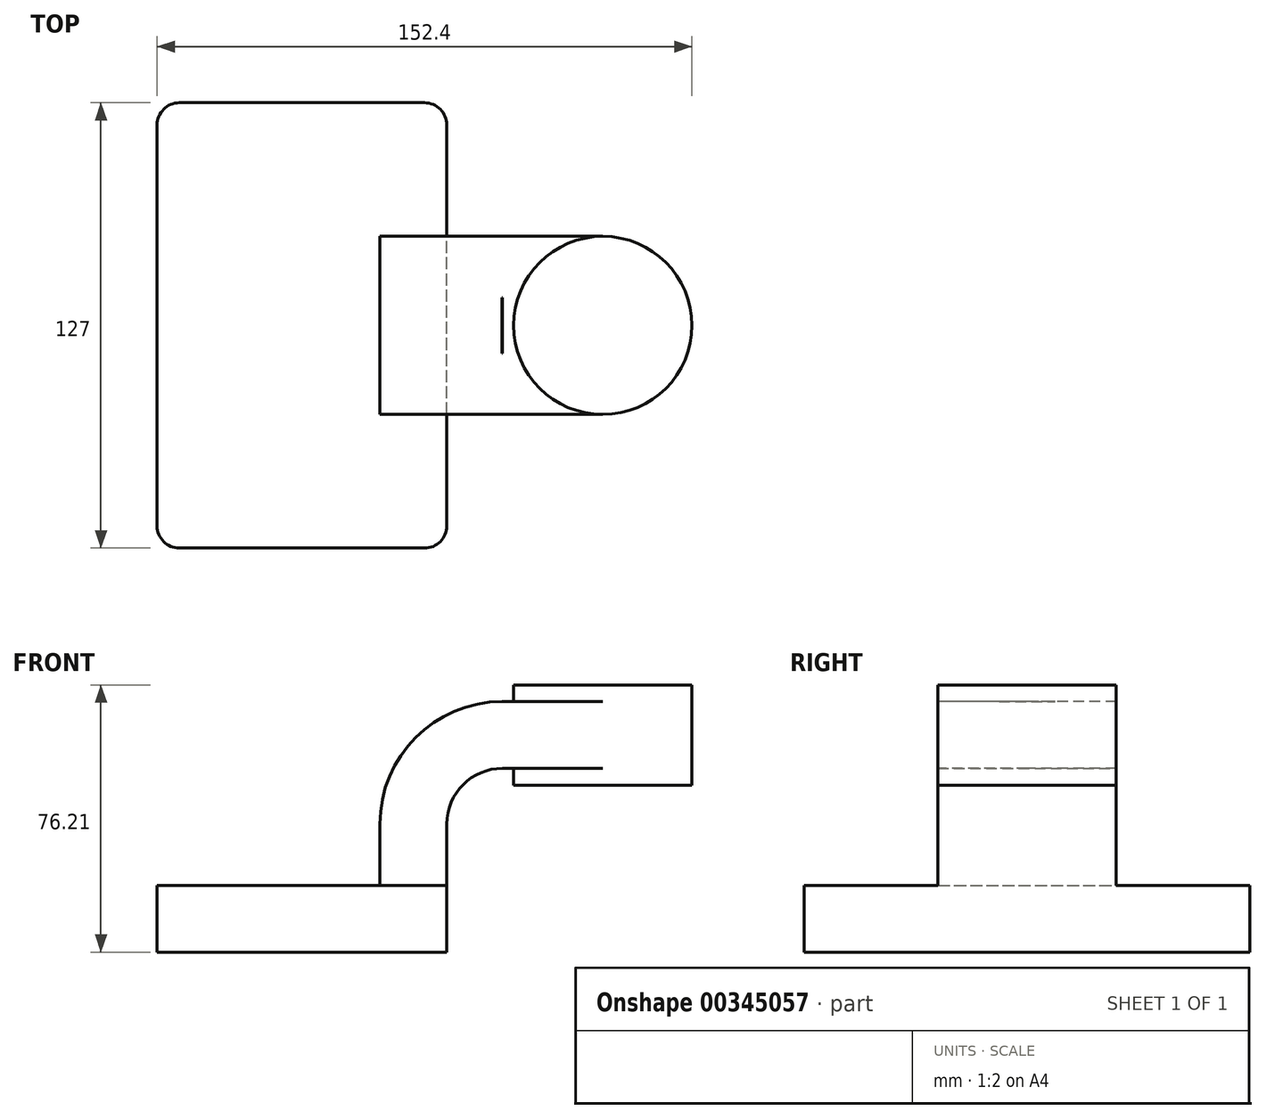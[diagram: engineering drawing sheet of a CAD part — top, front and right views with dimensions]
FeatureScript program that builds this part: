
annotation { "Feature Type Name" : "Feature", "Feature Type Description" : "" }
export const myFeature = defineFeature(function(context is Context, id is Id, definition is map)
    precondition{}
    {
        {
            var Q0;
            Q0=qCreatedBy(makeId("Front.planeOp"),FACE);
            var sketch = newSketch(context, id + "F0", { "sketchPlane" : qUnion([Q0])});
            skLineSegment(sketch, "E0.bottom", {"start": v(41.28, -9.52) * mm, "end": v(-41.28, -9.53) * mm});
            skLineSegment(sketch, "E0.top", {"start": v(41.28, 9.53) * mm, "end": v(-41.28, 9.53) * mm});
            skLineSegment(sketch, "E0.left", {"start": v(41.28, -9.52) * mm, "end": v(41.28, 9.53) * mm});
            skLineSegment(sketch, "E0.right", {"start": v(-41.28, -9.53) * mm, "end": v(-41.28, 9.53) * mm});
            skPoint(sketch, "E0.middle", {"position": v(0, 0) * mm});
            skLineSegment(sketch, "E1.bottom", {"start": v(60.32, 38.1) * mm, "end": v(111.12, 38.1) * mm});
            skLineSegment(sketch, "E1.top", {"start": v(60.32, 66.68) * mm, "end": v(111.12, 66.68) * mm});
            skLineSegment(sketch, "E1.left", {"start": v(60.32, 38.1) * mm, "end": v(60.32, 66.68) * mm});
            skLineSegment(sketch, "E1.right", {"start": v(111.12, 38.1) * mm, "end": v(111.12, 66.68) * mm});
            skPoint(sketch, "E1.middle", {"position": v(85.72, 52.39) * mm});
            skLineSegment(sketch, "E2", {"start": v(41.28, 9.53) * mm, "end": v(41.28, 27) * mm});
            skArc(sketch, "E3", {"start": v(41.27, 27) * mm, "mid": v(45.92, 38.23) * mm, "end": v(57.15, 42.88) * mm});
            skLineSegment(sketch, "E4", {"start": v(57.15, 42.88) * mm, "end": v(85.72, 42.88) * mm});
            skLineSegment(sketch, "E5.0", {"start": v(57.15, 61.93) * mm, "end": v(85.72, 61.93) * mm});
            skArc(sketch, "E5.1", {"start": v(22.23, 27) * mm, "mid": v(32.45, 51.7) * mm, "end": v(57.15, 61.93) * mm});
            skLineSegment(sketch, "E5.2", {"start": v(22.22, 9.53) * mm, "end": v(22.22, 27) * mm});
            skLineSegment(sketch, "E6", {"start": v(85.72, 42.88) * mm, "end": v(85.72, 61.93) * mm});
            skFitSpline(sketch, "E7", {"points": [v(-41.28, 9.52) * mm, v(57.15, 61.93) * mm], "startDerivative": vector(-0.5, 64.67) * mm, "endDerivative": vector(125.26, 0.2) * mm});
            skLineSegment(sketch, "E8", {"start": v(85.72, 38.1) * mm, "end": v(85.72, 66.68) * mm});
            skSolve(sketch);
        }
        {
            var Q0;
            Q0=makeQuery(id+"F0.imprint","IMPRINT",FACE,{"disambiguationData":[TD([[makeQuery(id+"F0.imprint","IMPRINT",EDGE,{"derivedFrom":sQuery(id+"F0.wireOp",EDGE,"E0.bottom")}),-1.0]])]});
            extrude(context, id + "F1", {"entities" : qUnion([Q0]), "endBound" : BoundingType.SYMMETRIC, "depth" : 127 * mm});
        }
        {
            var Q0;
            {var subQ1=sQuery(id+"F0.wireOp",EDGE,"E2");Q0=makeQuery(id+"F0.imprint","IMPRINT",FACE,{"disambiguationData":[TD([[makeQuery(id+"F0.imprint","IMPRINT",EDGE,{"derivedFrom":subQ1}),1.0]])]});}
            var Q1;
            {var subQ5=sQuery(id+"F0.wireOp",EDGE,"E6");Q1=makeQuery(id+"F0.imprint","IMPRINT",FACE,{"disambiguationData":[TD([[makeQuery(id+"F0.imprint","IMPRINT",EDGE,{"derivedFrom":subQ5}),1.0]])]});}
            extrude(context, id + "F2", {"entities" : qUnion([Q0, Q1]), "operationType" : NewBodyOperationType.ADD, "endBound" : BoundingType.SYMMETRIC, "depth" : 50.8 * mm});
        }
        {
            var Q0;
            Q0=makeQuery(id+"F0.imprint","IMPRINT",FACE,{"disambiguationData":[TD([[makeQuery(id+"F0.imprint","IMPRINT",EDGE,{"derivedFrom":sQuery(id+"F0.wireOp",EDGE,"E5.1")}),1.0]])]});
            extrude(context, id + "F3", {"entities" : qUnion([Q0]), "endBound" : BoundingType.SYMMETRIC, "depth" : 15.88 * mm});
        }
        {
            var Q0;
            {var subQ0=sQuery(id+"F0.wireOp",EDGE,"E4");var subQ1=sQuery(id+"F0.wireOp",EDGE,"E1.left");var subQ2=makeQuery(id+"F0.imprint","INTERSECT",VERTEX,{"derivedFrom":[subQ1,subQ0]});Q0=makeQuery(id+"F0.imprint","IMPRINT",FACE,{"disambiguationData":[TD([[makeQuery(id+"F0.imprint","IMPRINT",EDGE,{"disambiguationData":[TD([[subQ2,-1.0]])],"derivedFrom":subQ1}),-1.0]])]});}
            extrude(context, id + "F4", {"entities" : qUnion([Q0]), "operationType" : NewBodyOperationType.ADD, "endBound" : BoundingType.SYMMETRIC, "depth" : 50.8 * mm});
        }
        {
            var Q0;
            {var subQ4=sQuery(id+"F0.wireOp",EDGE,"E1.right");Q0=makeQuery(id+"F0.imprint","IMPRINT",FACE,{"disambiguationData":[TD([[makeQuery(id+"F0.imprint","IMPRINT",EDGE,{"derivedFrom":subQ4}),1.0]])]});}
            var Q1;
            Q1=sQuery(id+"F0.wireOp",EDGE,"E8");
            revolve(context, id + "F5", {"operationType" : NewBodyOperationType.ADD, "entities" : qUnion([Q0]), "axis" : qUnion([Q1]), "revolveType" : RevolveType.FULL});
        }
        {
            var Q0;
            Q0=makeQuery(id+"F1.opExtrude","CAP_EDGE",EDGE,{"disambiguationData":[OSD([sQuery(id+"F0.wireOp",EDGE,"E0.right")])],"isStart":false});
            var Q1;
            Q1=makeQuery(id+"F1.opExtrude","CAP_EDGE",EDGE,{"disambiguationData":[OSD([sQuery(id+"F0.wireOp",EDGE,"E0.left")])],"isStart":false});
            var Q2;
            Q2=makeQuery(id+"F1.opExtrude","CAP_EDGE",EDGE,{"disambiguationData":[OSD([sQuery(id+"F0.wireOp",EDGE,"E0.left")])],"isStart":true});
            var Q3;
            Q3=makeQuery(id+"F1.opExtrude","CAP_EDGE",EDGE,{"disambiguationData":[OSD([sQuery(id+"F0.wireOp",EDGE,"E0.right")])],"isStart":true});
            fillet(context, id + "F6", {"entities" : qUnion([Q0, Q1, Q2, Q3]), "radius" : 6.35 * mm, "tangentPropagation" : true, "allowEdgeOverflow" : false});
        }
    });
